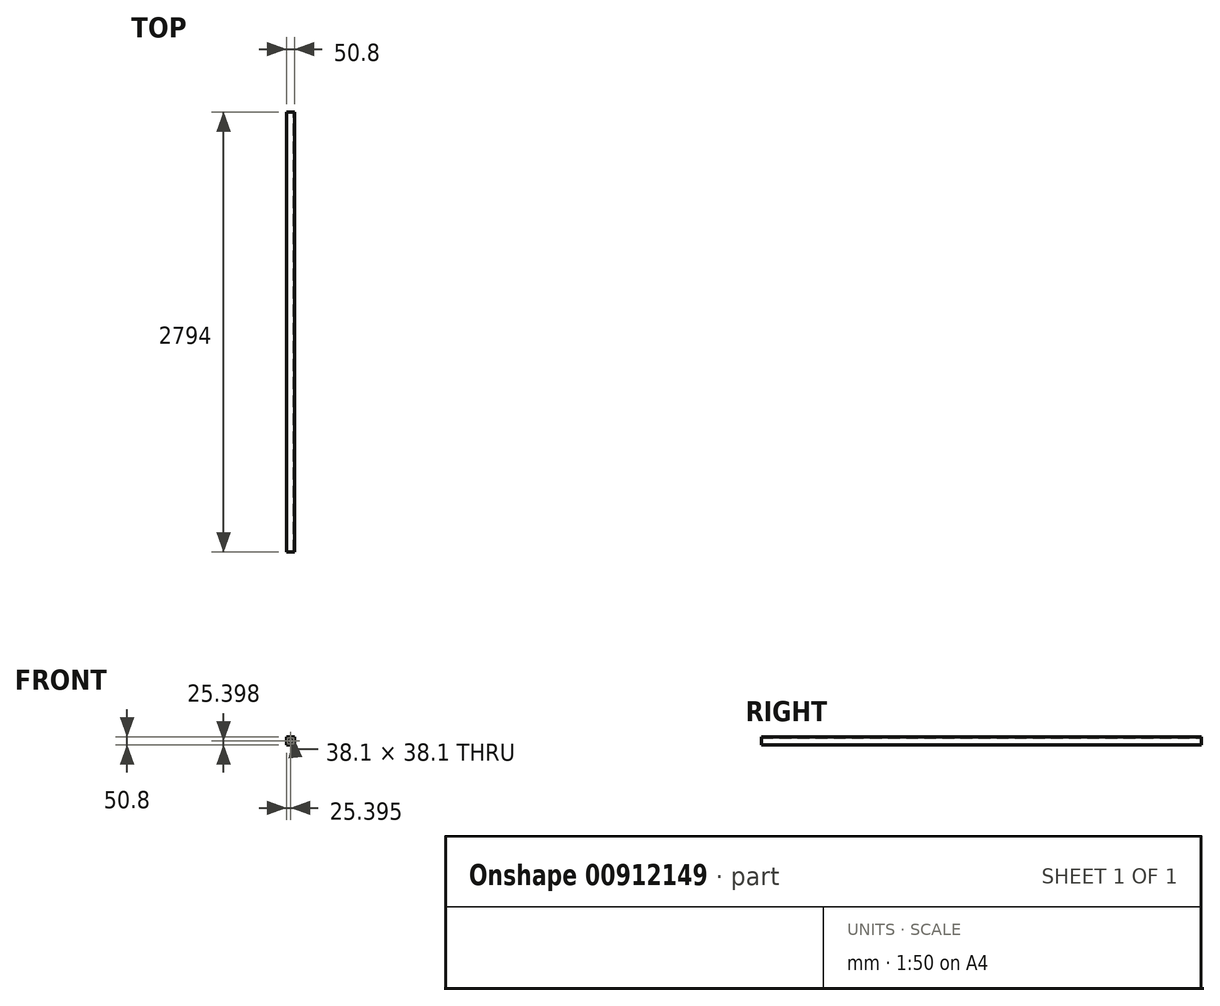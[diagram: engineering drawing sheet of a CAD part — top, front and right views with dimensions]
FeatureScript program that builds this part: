
annotation { "Feature Type Name" : "Feature", "Feature Type Description" : "" }
export const myFeature = defineFeature(function(context is Context, id is Id, definition is map)
    precondition{}
    {
        {
            var Q0;
            Q0=qCreatedBy(makeId("Front.planeOp"),FACE);
            var sketch = newSketch(context, id + "F0", { "sketchPlane" : qUnion([Q0])});
            skLineSegment(sketch, "E0.bottom", {"start": v(-37.95, 26.49) * mm, "end": v(12.85, 26.49) * mm});
            skLineSegment(sketch, "E0.top", {"start": v(-37.95, -24.31) * mm, "end": v(12.85, -24.31) * mm});
            skLineSegment(sketch, "E0.left", {"start": v(-37.95, 26.49) * mm, "end": v(-37.95, -24.31) * mm});
            skLineSegment(sketch, "E0.right", {"start": v(12.85, 26.49) * mm, "end": v(12.85, -24.31) * mm});
            skLineSegment(sketch, "E1.0", {"start": v(6.5, 20.14) * mm, "end": v(6.5, -17.96) * mm});
            skLineSegment(sketch, "E1.1", {"start": v(-31.6, 20.14) * mm, "end": v(6.5, 20.14) * mm});
            skLineSegment(sketch, "E1.2", {"start": v(-31.6, 20.14) * mm, "end": v(-31.6, -17.96) * mm});
            skLineSegment(sketch, "E1.3", {"start": v(-31.6, -17.96) * mm, "end": v(6.5, -17.96) * mm});
            skSolve(sketch);
        }
        {
            var Q0;
            Q0=makeQuery(id+"F0.imprint","IMPRINT",FACE,{"disambiguationData":[TD([[makeQuery(id+"F0.imprint","IMPRINT",EDGE,{"derivedFrom":sQuery(id+"F0.wireOp",EDGE,"E0.bottom")}),-1.0]])]});
            extrude(context, id + "F1", {"entities" : qUnion([Q0]), "depth" : 2794 * mm, "offsetDistance" : 25.4 * mm});
        }
    });
